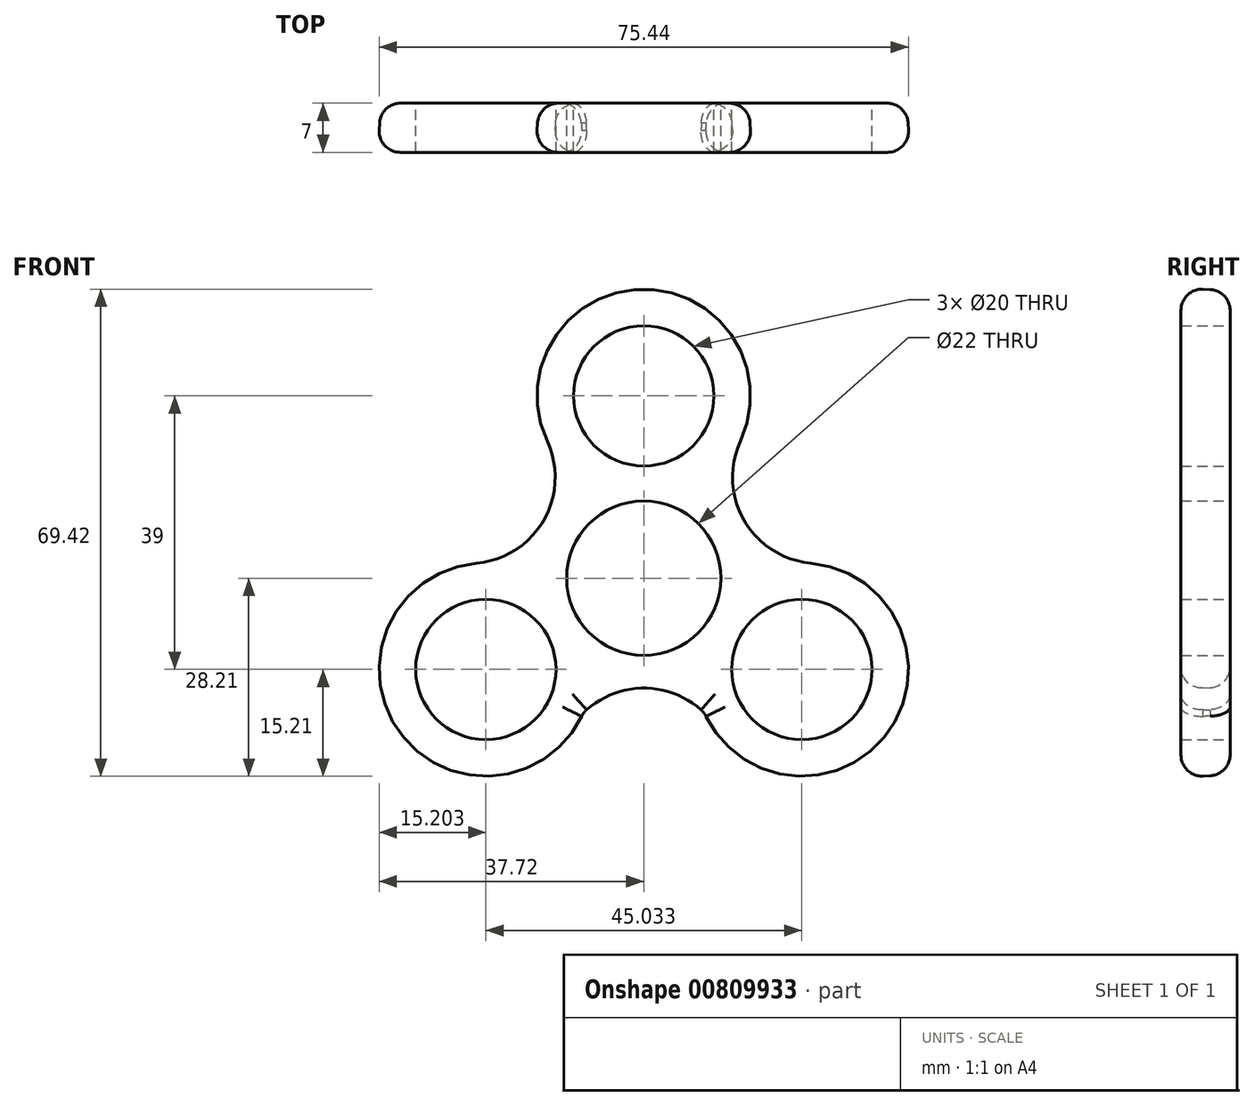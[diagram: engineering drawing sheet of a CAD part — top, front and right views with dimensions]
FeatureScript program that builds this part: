
annotation { "Feature Type Name" : "Feature", "Feature Type Description" : "" }
export const myFeature = defineFeature(function(context is Context, id is Id, definition is map)
    precondition{}
    {
        {
            var Q0;
            Q0=qCreatedBy(makeId("Front.planeOp"),FACE);
            var sketch = newSketch(context, id + "F0", { "sketchPlane" : qUnion([Q0])});
            skCircle(sketch, "E0", {"center": v(0, 0) * mm, "radius": 26 * mm, "construction": true});
            skCircle(sketch, "E1", {"center": v(0, 26) * mm, "radius": 15 * mm});
            skCircle(sketch, "E2", {"center": v(22.52, -13) * mm, "radius": 15 * mm});
            skCircle(sketch, "E3", {"center": v(-22.52, -13) * mm, "radius": 15 * mm});
            skLineSegment(sketch, "E4", {"start": v(0, 0) * mm, "end": v(-58.37, -33.7) * mm, "construction": true});
            skLineSegment(sketch, "E5", {"start": v(0, 0) * mm, "end": v(56.56, -32.65) * mm, "construction": true});
            skArc(sketch, "E6", {"start": v(-23.83, 1.94) * mm, "mid": v(-14.1, 8.14) * mm, "end": v(-13.6, 19.67) * mm});
            skArc(sketch, "E7", {"start": v(13.6, 19.67) * mm, "mid": v(14.1, 8.14) * mm, "end": v(23.83, 1.94) * mm});
            skArc(sketch, "E8", {"start": v(11.59, -23.27) * mm, "mid": v(0, -15.46) * mm, "end": v(-11.59, -23.27) * mm});
            skSolve(sketch);
        }
        {
            var Q0;
            {var subQ0=sQuery(id+"F0.wireOp",EDGE,"E1");var subQ1=makeQuery(id+"F0.imprint","INTERSECT",VERTEX,{"derivedFrom":[subQ0,sQuery(id+"F0.wireOp",EDGE,"E6")]});Q0=makeQuery(id+"F0.imprint","IMPRINT",FACE,{"disambiguationData":[TD([[makeQuery(id+"F0.imprint","IMPRINT",EDGE,{"disambiguationData":[TD([[subQ1,-1.0]])],"derivedFrom":subQ0}),1.0]])]});}
            var Q1;
            {var subQ0=sQuery(id+"F0.wireOp",EDGE,"E2");var subQ1=makeQuery(id+"F0.imprint","INTERSECT",VERTEX,{"derivedFrom":[subQ0,sQuery(id+"F0.wireOp",EDGE,"E7")]});Q1=makeQuery(id+"F0.imprint","IMPRINT",FACE,{"disambiguationData":[TD([[makeQuery(id+"F0.imprint","IMPRINT",EDGE,{"disambiguationData":[TD([[subQ1,-1.0]])],"derivedFrom":subQ0}),1.0]])]});}
            var Q2;
            {var subQ0=sQuery(id+"F0.wireOp",EDGE,"E6");Q2=makeQuery(id+"F0.imprint","IMPRINT",FACE,{"disambiguationData":[TD([[makeQuery(id+"F0.imprint","IMPRINT",EDGE,{"derivedFrom":subQ0}),-1.0]])]});}
            var Q3;
            {var subQ0=sQuery(id+"F0.wireOp",EDGE,"E8");var subQ1=sQuery(id+"F0.wireOp",EDGE,"E3");var subQ2=makeQuery(id+"F0.imprint","INTERSECT",VERTEX,{"disambiguationData":[OD(0.0)],"derivedFrom":[subQ1,subQ0]});Q3=makeQuery(id+"F0.imprint","IMPRINT",FACE,{"disambiguationData":[TD([[makeQuery(id+"F0.imprint","IMPRINT",EDGE,{"disambiguationData":[TD([[subQ2,-1.0]])],"derivedFrom":subQ1}),1.0]])]});}
            var Q4;
            {var subQ0=sQuery(id+"F0.wireOp",EDGE,"E8");var subQ1=sQuery(id+"F0.wireOp",EDGE,"E2");var subQ2=makeQuery(id+"F0.imprint","INTERSECT",VERTEX,{"disambiguationData":[OD(0.0)],"derivedFrom":[subQ1,subQ0]});Q4=makeQuery(id+"F0.imprint","IMPRINT",FACE,{"disambiguationData":[TD([[makeQuery(id+"F0.imprint","IMPRINT",EDGE,{"disambiguationData":[TD([[subQ2,1.0]])],"derivedFrom":subQ1}),1.0]])]});}
            var Q5;
            {var subQ0=sQuery(id+"F0.wireOp",EDGE,"E3");var subQ1=makeQuery(id+"F0.imprint","INTERSECT",VERTEX,{"derivedFrom":[subQ0,sQuery(id+"F0.wireOp",EDGE,"E6")]});Q5=makeQuery(id+"F0.imprint","IMPRINT",FACE,{"disambiguationData":[TD([[makeQuery(id+"F0.imprint","IMPRINT",EDGE,{"disambiguationData":[TD([[subQ1,-1.0]])],"derivedFrom":subQ0}),1.0]])]});}
            extrude(context, id + "F1", {"entities" : qUnion([Q0, Q1, Q2, Q3, Q4, Q5]), "depth" : 7 * mm, "offsetDistance" : 25 * mm, "hasDraft" : true, "draftAngle" : 3 * degree});
        }
        {
            var Q0;
            Q0=makeQuery(id+"F1.opExtrude","CAP_EDGE",EDGE,{"disambiguationData":[OSD([sQuery(id+"F0.wireOp",EDGE,"E7")])],"isStart":false});
            var Q1;
            Q1=makeQuery(id+"F1.opExtrude","CAP_EDGE",EDGE,{"disambiguationData":[OSD([sQuery(id+"F0.wireOp",EDGE,"E3")])],"isStart":false});
            var Q2;
            Q2=makeQuery(id+"F1.opExtrude","CAP_EDGE",EDGE,{"disambiguationData":[OSD([sQuery(id+"F0.wireOp",EDGE,"E1")])],"isStart":false});
            var Q3;
            Q3=makeQuery(id+"F1.opExtrude","CAP_EDGE",EDGE,{"disambiguationData":[OSD([sQuery(id+"F0.wireOp",EDGE,"E1")])],"isStart":true});
            var Q4;
            Q4=makeQuery(id+"F1.opExtrude","CAP_EDGE",EDGE,{"disambiguationData":[OSD([sQuery(id+"F0.wireOp",EDGE,"E8")])],"isStart":true});
            var Q5;
            Q5=makeQuery(id+"F1.opExtrude","CAP_EDGE",EDGE,{"disambiguationData":[OSD([sQuery(id+"F0.wireOp",EDGE,"E8")])],"isStart":false});
            var Q6;
            Q6=makeQuery(id+"F1.opExtrude","CAP_EDGE",EDGE,{"disambiguationData":[OSD([sQuery(id+"F0.wireOp",EDGE,"E3")])],"isStart":true});
            var Q7;
            Q7=makeQuery(id+"F1.opExtrude","CAP_EDGE",EDGE,{"disambiguationData":[OSD([sQuery(id+"F0.wireOp",EDGE,"E2")])],"isStart":false});
            var Q8;
            Q8=makeQuery(id+"F1.opExtrude","CAP_EDGE",EDGE,{"disambiguationData":[OSD([sQuery(id+"F0.wireOp",EDGE,"E2")])],"isStart":true});
            var Q9;
            Q9=makeQuery(id+"F1.opExtrude","SWEPT_EDGE",EDGE,{"disambiguationData":[OSD([sQuery(id+"F0.wireOp",EDGE,"E3"),sQuery(id+"F0.wireOp",EDGE,"E8")])]});
            var Q10;
            Q10=makeQuery(id+"F1.opExtrude","SWEPT_EDGE",EDGE,{"disambiguationData":[OSD([sQuery(id+"F0.wireOp",EDGE,"E2"),sQuery(id+"F0.wireOp",EDGE,"E8")])]});
            var Q11;
            Q11=makeQuery(id+"F1.opExtrude","SWEPT_EDGE",EDGE,{"disambiguationData":[OSD([sQuery(id+"F0.wireOp",EDGE,"E2"),sQuery(id+"F0.wireOp",EDGE,"E7")])]});
            var Q12;
            Q12=makeQuery(id+"F1.opExtrude","SWEPT_EDGE",EDGE,{"disambiguationData":[OSD([sQuery(id+"F0.wireOp",EDGE,"E1"),sQuery(id+"F0.wireOp",EDGE,"E7")])]});
            var Q13;
            Q13=makeQuery(id+"F1.opExtrude","CAP_EDGE",EDGE,{"disambiguationData":[OSD([sQuery(id+"F0.wireOp",EDGE,"E6")])],"isStart":false});
            var Q14;
            Q14=makeQuery(id+"F1.opExtrude","CAP_EDGE",EDGE,{"disambiguationData":[OSD([sQuery(id+"F0.wireOp",EDGE,"E6")])],"isStart":true});
            var Q15;
            Q15=makeQuery(id+"F1.opExtrude","SWEPT_EDGE",EDGE,{"disambiguationData":[OSD([sQuery(id+"F0.wireOp",EDGE,"E1"),sQuery(id+"F0.wireOp",EDGE,"E6")])]});
            var Q16;
            Q16=makeQuery(id+"F1.opExtrude","SWEPT_EDGE",EDGE,{"disambiguationData":[OSD([sQuery(id+"F0.wireOp",EDGE,"E3"),sQuery(id+"F0.wireOp",EDGE,"E6")])]});
            var Q17;
            Q17=makeQuery(id+"F1.opExtrude","CAP_EDGE",EDGE,{"disambiguationData":[OSD([sQuery(id+"F0.wireOp",EDGE,"E7")])],"isStart":true});
            fillet(context, id + "F2", {"entities" : qUnion([Q0, Q1, Q2, Q3, Q4, Q5, Q6, Q7, Q8, Q9, Q10, Q11, Q12, Q13, Q14, Q15, Q16, Q17]), "radius" : 3 * mm, "tangentPropagation" : true, "allowEdgeOverflow" : false});
        }
        {
            var Q0;
            Q0=makeQuery(id+"F1.opExtrude","CAP_FACE",FACE,{"disambiguationData":[OSD([sQuery(id+"F0.wireOp",EDGE,"E1"),sQuery(id+"F0.wireOp",EDGE,"E2"),sQuery(id+"F0.wireOp",EDGE,"E3"),sQuery(id+"F0.wireOp",EDGE,"E6"),sQuery(id+"F0.wireOp",EDGE,"E7"),sQuery(id+"F0.wireOp",EDGE,"E8")])],"isStart":true});
            var sketch = newSketch(context, id + "F3", { "sketchPlane" : qUnion([Q0])});
            skPoint(sketch, "E9", {"position": v(22.52, -13) * mm});
            skPoint(sketch, "E10", {"position": v(0, 26) * mm});
            skPoint(sketch, "E11", {"position": v(-22.52, -13) * mm});
            skPoint(sketch, "E12", {"position": v(0, 0) * mm});
            skSolve(sketch);
        }
        {
            var Q0;
            Q0=sQuery(id+"F3.wireOp",VERTEX,"E10");
            var Q1;
            Q1=sQuery(id+"F3.wireOp",VERTEX,"E9");
            var Q2;
            Q2=sQuery(id+"F3.wireOp",VERTEX,"E11");
            var Q3;
            Q3=makeQuery(id+"F1.opExtrude","SWEPT_BODY",BODY,{"disambiguationData":[OSD([sQuery(id+"F0.wireOp",EDGE,"E1"),sQuery(id+"F0.wireOp",EDGE,"E2"),sQuery(id+"F0.wireOp",EDGE,"E3"),sQuery(id+"F0.wireOp",EDGE,"E6"),sQuery(id+"F0.wireOp",EDGE,"E7"),sQuery(id+"F0.wireOp",EDGE,"E8")])]});
            hole(context, id + "F4", {"style" : HoleStyle.SIMPLE, "endStyle" : HoleEndStyle.THROUGH, "holeDiameter" : 20 * mm, "majorDiameter" : 5 * mm, "isTappedThrough" : true, "tappedDepth" : 12 * mm, "tapClearance" : 3, "locations" : qUnion([Q0, Q1, Q2]), "scope" : qUnion([Q3])});
        }
        {
            var Q0;
            Q0=makeQuery(id+"F1.opExtrude","CAP_FACE",FACE,{"disambiguationData":[OSD([sQuery(id+"F0.wireOp",EDGE,"E1"),sQuery(id+"F0.wireOp",EDGE,"E2"),sQuery(id+"F0.wireOp",EDGE,"E3"),sQuery(id+"F0.wireOp",EDGE,"E6"),sQuery(id+"F0.wireOp",EDGE,"E7"),sQuery(id+"F0.wireOp",EDGE,"E8")])],"isStart":true});
            var sketch = newSketch(context, id + "F5", { "sketchPlane" : qUnion([Q0])});
            skPoint(sketch, "E13", {"position": v(0, 0) * mm});
            skSolve(sketch);
        }
        {
            var Q0;
            Q0=sQuery(id+"F5.wireOp",VERTEX,"E13");
            var Q1;
            Q1=makeQuery(id+"F1.opExtrude","SWEPT_BODY",BODY,{"disambiguationData":[OSD([sQuery(id+"F0.wireOp",EDGE,"E1"),sQuery(id+"F0.wireOp",EDGE,"E2"),sQuery(id+"F0.wireOp",EDGE,"E3"),sQuery(id+"F0.wireOp",EDGE,"E6"),sQuery(id+"F0.wireOp",EDGE,"E7"),sQuery(id+"F0.wireOp",EDGE,"E8")])]});
            hole(context, id + "F6", {"style" : HoleStyle.SIMPLE, "endStyle" : HoleEndStyle.THROUGH, "holeDiameter" : 22 * mm, "majorDiameter" : 5 * mm, "isTappedThrough" : true, "tappedDepth" : 12 * mm, "tapClearance" : 3, "locations" : qUnion([Q0]), "scope" : qUnion([Q1])});
        }
    });
